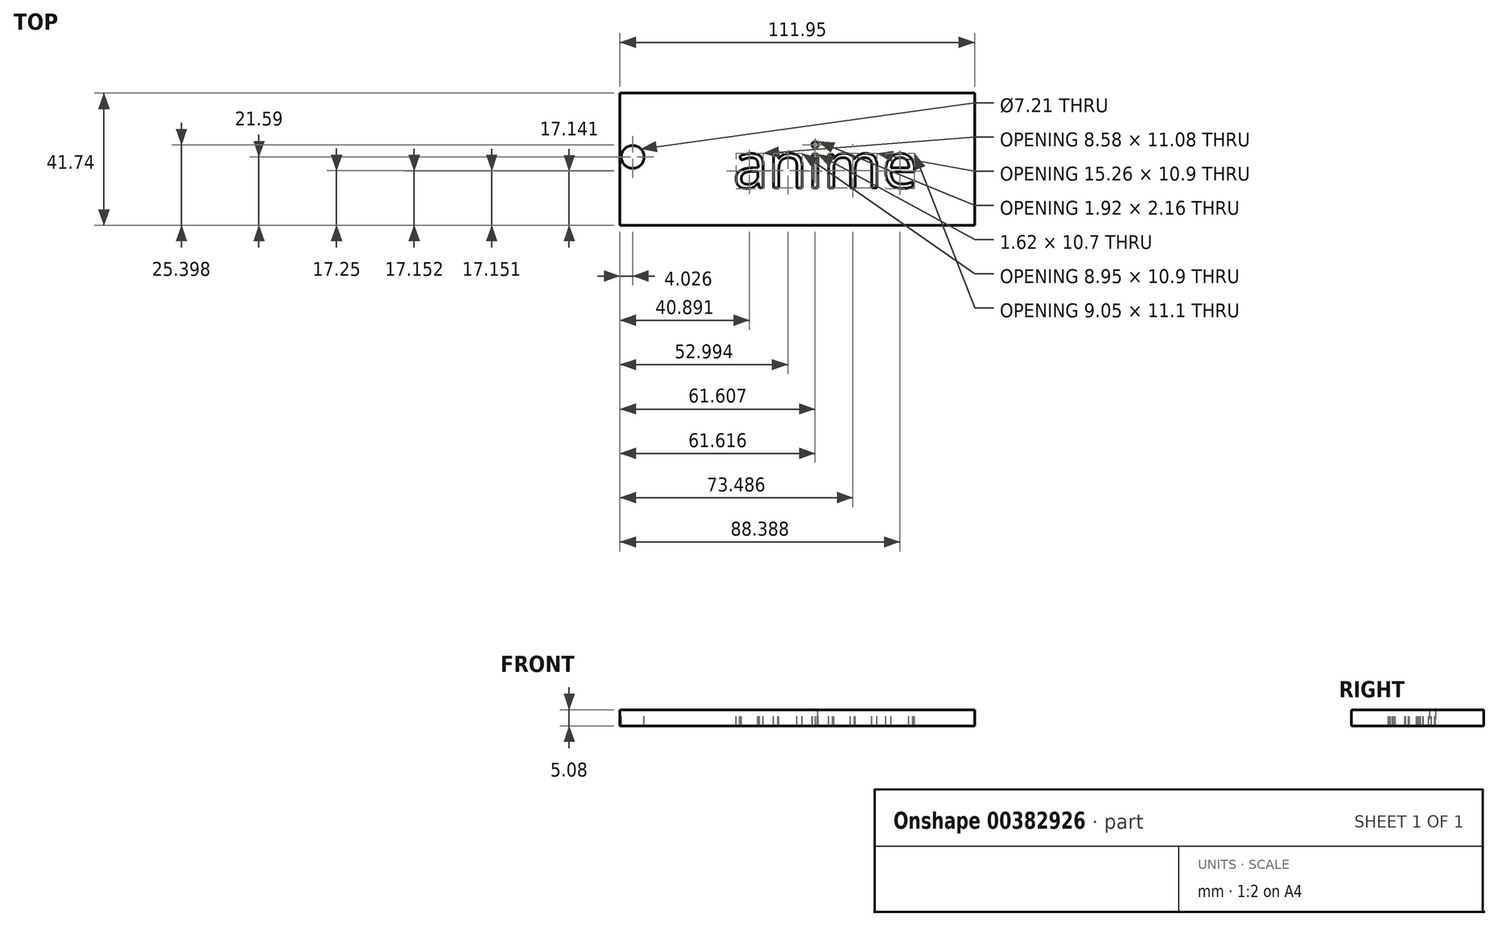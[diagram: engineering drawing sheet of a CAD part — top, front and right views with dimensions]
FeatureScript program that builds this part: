
annotation { "Feature Type Name" : "Feature", "Feature Type Description" : "" }
export const myFeature = defineFeature(function(context is Context, id is Id, definition is map)
    precondition{}
    {
        {
            var Q0;
            Q0=qCreatedBy(makeId("Top.planeOp"),FACE);
            var sketch = newSketch(context, id + "F0", { "sketchPlane" : qUnion([Q0])});
            skLineSegment(sketch, "E0.bottom", {"start": v(-48.06, 22.74) * mm, "end": v(63.9, 22.74) * mm});
            skLineSegment(sketch, "E0.top", {"start": v(-48.06, -19) * mm, "end": v(63.9, -19) * mm});
            skLineSegment(sketch, "E0.left", {"start": v(-48.06, 22.74) * mm, "end": v(-48.06, -19) * mm});
            skLineSegment(sketch, "E0.right", {"start": v(63.9, 22.74) * mm, "end": v(63.9, -19) * mm});
            skSolve(sketch);
        }
        {
            var Q0;
            Q0=makeQuery(id+"F0.imprint","IMPRINT",FACE,{"disambiguationData":[TD([[makeQuery(id+"F0.imprint","IMPRINT",EDGE,{"derivedFrom":sQuery(id+"F0.wireOp",EDGE,"E0.bottom")}),-1.0]])]});
            extrude(context, id + "F1", {"entities" : qUnion([Q0]), "depth" : 5.08 * mm});
        }
        {
            var Q0;
            Q0=makeQuery(id+"F1.opExtrude","CAP_FACE",FACE,{"disambiguationData":[OSD([sQuery(id+"F0.wireOp",EDGE,"E0.bottom"),sQuery(id+"F0.wireOp",EDGE,"E0.top"),sQuery(id+"F0.wireOp",EDGE,"E0.left"),sQuery(id+"F0.wireOp",EDGE,"E0.right")])],"isStart":false});
            var sketch = newSketch(context, id + "F2", { "sketchPlane" : qUnion([Q0])});
            skCircle(sketch, "E1", {"center": v(-44.03, 2.6) * mm, "radius": 3.6 * mm});
            skText(sketch, "E2", { "text": "anime", "fontName": "OpenSans-Regular.ttf"});
            const initialGuessF2  = {"E2": [-0.01238, -0.0072, 1, 0, 0.0144]};
            skSetInitialGuess(sketch, initialGuessF2);
            skSolve(sketch);
        }
        {
            var Q0;
            Q0 = qSketchRegion(id + "F2", true);
            extrude(context, id + "F3", {"entities" : qUnion([Q0]), "operationType" : NewBodyOperationType.REMOVE, "oppositeDirection" : true, "depth" : 25.4 * mm});
        }
    });
